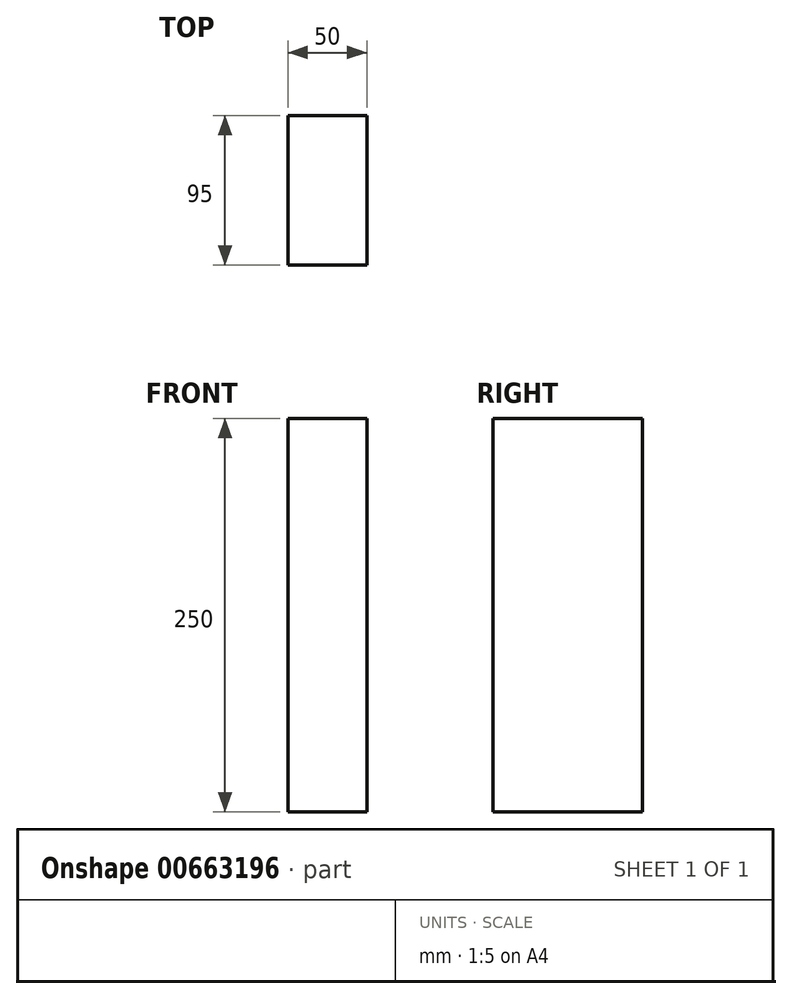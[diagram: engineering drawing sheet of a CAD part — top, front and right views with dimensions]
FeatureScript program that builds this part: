
annotation { "Feature Type Name" : "Feature", "Feature Type Description" : "" }
export const myFeature = defineFeature(function(context is Context, id is Id, definition is map)
    precondition{}
    {
        {
            var Q0;
            Q0=qCreatedBy(makeId("Top.planeOp"),FACE);
            var sketch = newSketch(context, id + "F0", { "sketchPlane" : qUnion([Q0])});
            skLineSegment(sketch, "E0.bottom", {"start": v(25, 47.5) * mm, "end": v(-25, 47.5) * mm});
            skLineSegment(sketch, "E0.top", {"start": v(25, -47.5) * mm, "end": v(-25, -47.5) * mm});
            skLineSegment(sketch, "E0.left", {"start": v(25, 47.5) * mm, "end": v(25, -47.5) * mm});
            skLineSegment(sketch, "E0.right", {"start": v(-25, 47.5) * mm, "end": v(-25, -47.5) * mm});
            skPoint(sketch, "E0.middle", {"position": v(0, 0) * mm});
            skSolve(sketch);
        }
        {
            var Q0;
            Q0=makeQuery(id+"F0.imprint","IMPRINT",FACE,{"disambiguationData":[TD([[makeQuery(id+"F0.imprint","IMPRINT",EDGE,{"derivedFrom":sQuery(id+"F0.wireOp",EDGE,"E0.bottom")}),1.0]])]});
            extrude(context, id + "F1", {"entities" : qUnion([Q0]), "endBound" : BoundingType.SYMMETRIC, "depth" : 250 * mm, "offsetDistance" : 25 * mm});
        }
    });
